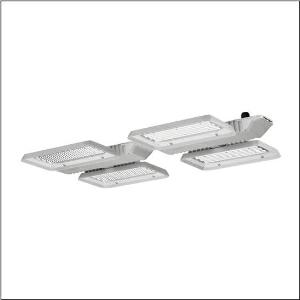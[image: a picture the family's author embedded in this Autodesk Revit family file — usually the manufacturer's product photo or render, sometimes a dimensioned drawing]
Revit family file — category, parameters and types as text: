
# Revit family: highbay_11_51hla2d24mca
name_source: partatom
category: Lighting Fixtures
units: mm (PartAtom-declared; Revit-internal decimal feet)

## family parameters
Cut with Voids When Loaded = No
Host = Face
Light Source = No
Part Type = Normal
Room Calculation Point = No
Round Connector Dimension = Use Diameter
Shared = No

## types (1)
- --- (1 x LED, 28800 lm, 162.4 W, 4000K)
    Apparent Load = 162 VA
    CIE Flux Codes = 89 96 99 100 100
    Color Rendering = 80
    Color Temperature = 4000K
    Default Elevation = 1800 mm
    Description = Highbay 11, LED high bay luminaire, primary light control with lens, of PMMA, light emission: direct distribution, primary light characteristic: symmetric, installation type: surface-mounted, suspended mounting, for 2x 2x LED, rated luminous flux: 28.800lm, luminous efficacy: 177lm/W, light colour: 840, colour temperature: 4000K, control gear: DALI (with two DALI addresses), with terminal, 5-pole, max. 2.5mm², mains connection: 230..240V, AC, 50/60Hz, rated input power: 162W, LED unit, of diecast aluminium, unplated, bead blasted, silver, length: 940mm, width: 500mm, height: 65mm, housing, of diecast aluminium, uncoated, bead blasted, silver, protection rating (complete): IP65, insulation class (complete): insulation class I (protective earthing), certification: CE, ENEC, VDE, UKCA, protection symbol: D, impact resistance: IK08 with glass or PC cover, permissible operating ambient temperature: -35..+55°C, reducing of maximum allowable ambient temperature of 5°C with ceiling mounting, corresponds to IFS (International Featured Standards) requirements for safety and quality in the food industry, packaging unit: 1 piece
    Height = 95 mm
    Lamp = 1 x LED
    Lamp Light Flux = 28800 lm
    Lamp Power = 162.4 W
    Lamp count = 1
    Length = 939 mm
    Luminous efficacy = 177 lm/W
    Manufacturer = Siteco
    ModVariant = No
    Model = 51HLA2D24MCA
    Mounting Place = Ceiling
    Mounting Type = Pendant
    Number of Poles = 1
    OnlyDefault = Yes
    Power Factor = 1
    Product Name = Highbay 11
    Product group = LED high bay luminaire
    ProductGroupID = 903
    Protection Class = Protection class I
    Protection Degree = IP 65
    RLX_Detail_Level = 1
    RLX_Emergency_Light_Flux = 0 lm
    RLX_Emergency_Type = 0
    RLX_Emergency_Type_DB = No
    RlxData = <blob elided: 96877 chars, md5=8d449e62>
    Socket = socket
    Standby Power = 0 W
    System Light Flux = 28800 lm
    System Power = 162 W
    Type Comments = factory setting: luminous flux: 100 % | dim-lin: 254 | 460 mA
    Type Image = l_1003428.jpg
    URL = http://relux.com
    VarID = @adj_201392
    Voltage = 0 V
    Weight = 0.00 kg
    Width = 501 mm

## geometry (parser evidence)
native form markers: Blend x4, Sweep x13
no freeform markers — native parametric forms only
